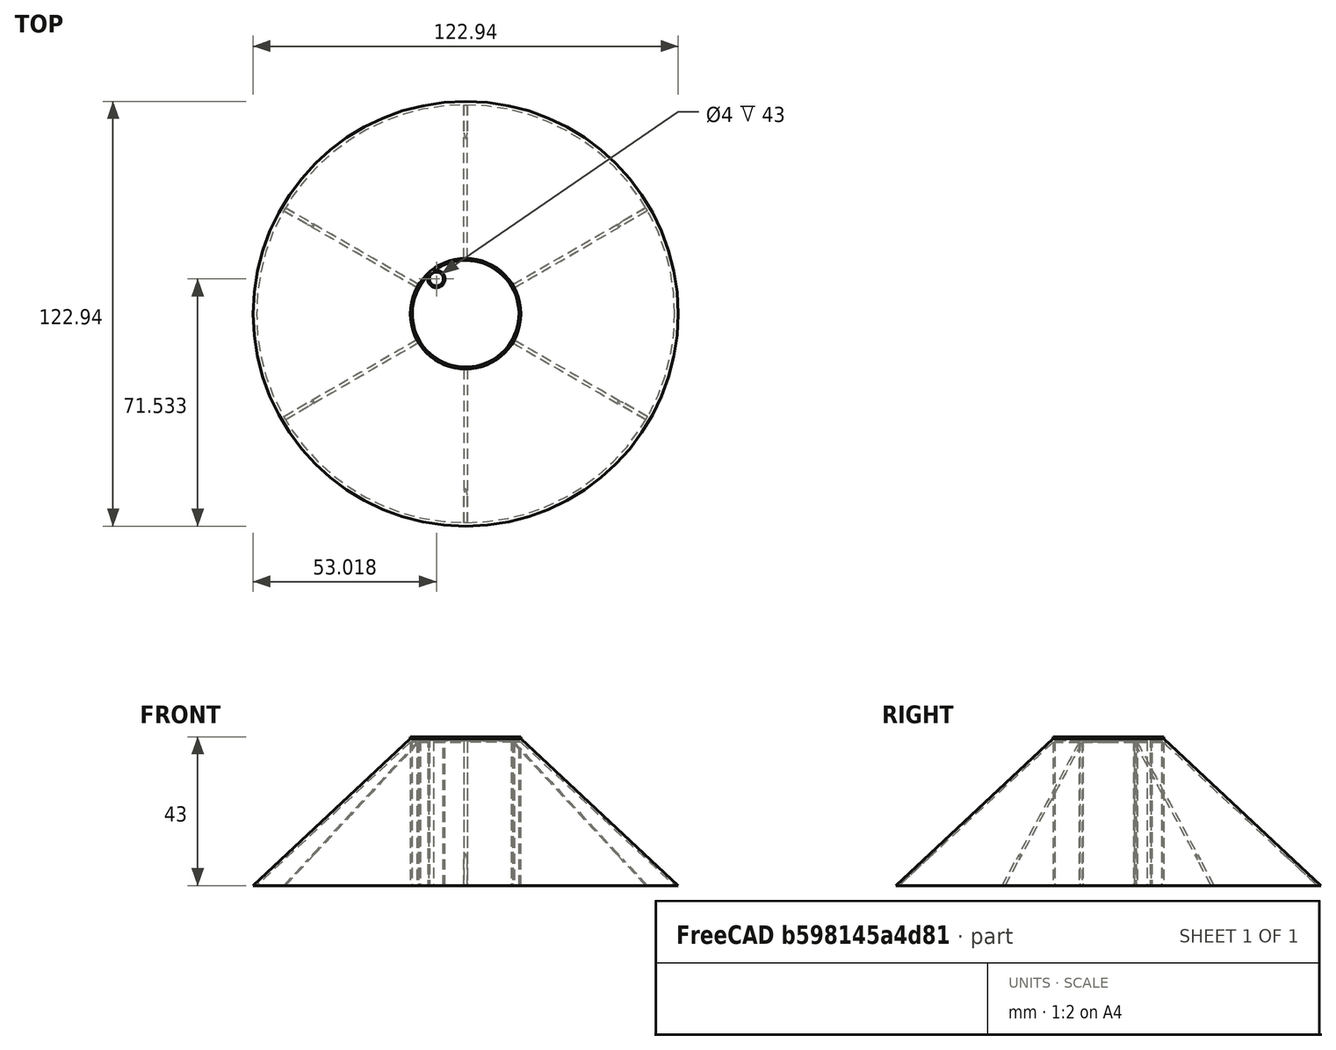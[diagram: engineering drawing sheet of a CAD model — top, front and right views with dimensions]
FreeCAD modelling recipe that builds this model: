
FCSTD DOCUMENT  (FreeCAD 0.20R29603 (Git))
Label: Ez3D-Mini-SaucerX2
License: All rights reserved
LicenseURL: http://en.wikipedia.org/wiki/All_rights_reserved
objects: Sketcher::SketchObject×4, PartDesign::Pad×3, Mesh::Feature×2, PartDesign::PolarPattern×1, PartDesign::Revolution×1, PartDesign::Body×1
note: 14 computed .brp shape members not serialized (recipe doc carries the construction recipe); baked Part::Feature solids carry a one-line shape summary decoded from their .brp

FEATURE [Mesh::Feature] Ez3D_13mmMotorTubeOnly_Body  label="Ez3D-13mmMotorTubeOnly-Body"
  Placement = pos=(-7.5,0,0) rot=(0,0,1;0rad)
FEATURE [Mesh::Feature] Ez3D_13mmMotorTubeOnly_Body001  label="Ez3D-13mmMotorTubeOnly-Body001"
  Placement = pos=(7.5,0,0) rot=(0,0,1;0rad)
FEATURE [Sketcher::SketchObject] Sketch  label="Center Support Structure"
  FullyConstrained = true
  MapMode = 5
  Support = -> [XY_Plane]
  sketch-geometry (2):
    g0: Circle CenterX=0 CenterY=0 CenterZ=0 NormalX=0 NormalY=0 NormalZ=1 AngleXU=0 Radius=15.5
    g1: Circle CenterX=0 CenterY=0 CenterZ=0 NormalX=0 NormalY=0 NormalZ=1 AngleXU=0 Radius=16
  constraints (4):
    c: Coincident(g0,g-1)
    c: Coincident(g1,g0)
    c: Diameter(g0) = 31
    c: Diameter(g1) = 32
FEATURE [PartDesign::Pad] Pad
  Direction = (0,0,1)
  Length = 43
  Length2 = 10
  Profile = -> Sketch
  ReferenceAxis = -> Sketch [N_Axis]
  Type = 0
FEATURE [Sketcher::SketchObject] Sketch001  label=""Fins""
  FullyConstrained = true
  MapMode = 5
  Placement = pos=(0,0,0) rot=(0.57735,0.57735,0.57735;2.0944rad)
  Support = -> [YZ_Plane]
  sketch-geometry (3):
    g0: LineSegment StartX=15.455 StartY=42 StartZ=0 EndX=15.455 EndY=0 EndZ=0
    g1: LineSegment StartX=15.455 StartY=0 StartZ=0 EndX=60.455 EndY=0 EndZ=0
    g2: LineSegment StartX=60.455 StartY=0 StartZ=0 EndX=15.455 EndY=42 EndZ=0
  constraints (9):
    c: Vertical(g0)
    c: Coincident(g0,g1)
    c: PointOnObject(g1,g-1)
    c: Horizontal(g1)
    c: Coincident(g1,g2)
    c: Coincident(g2,g0)
    c: DistanceY(g0,g0) = 42
    c: DistanceX(g-1,g0) = 15.455
    c: DistanceX(g1,g1) = 45
FEATURE [PartDesign::Pad] Pad001
  BaseFeature = -> Pad
  Direction = (1,-2e-16,3e-16)
  Length = 1
  Length2 = 10
  Midplane = true
  Profile = -> Sketch001
  ReferenceAxis = -> Sketch001 [N_Axis]
  Type = 0
FEATURE [PartDesign::PolarPattern] PolarPattern
  Angle = 360
  Axis = -> Z_Axis
  BaseFeature = -> Pad001
  Occurrences = 6
  Originals = -> [Pad001]
FEATURE [Sketcher::SketchObject] Sketch002  label="Top"
  FullyConstrained = false
  MapMode = 5
  Placement = pos=(0,0,0) rot=(0.57735,0.57735,0.57735;2.0944rad)
  Support = -> [YZ_Plane]
  sketch-geometry (4):
    g0: LineSegment StartX=15.445 StartY=42.9655 StartZ=0 EndX=15.445 EndY=41.9655 EndZ=0
    g1: LineSegment StartX=15.445 StartY=41.9655 StartZ=0 EndX=60.468 EndY=0 EndZ=0
    g2: LineSegment StartX=60.468 StartY=0 StartZ=0 EndX=61.468 EndY=0 EndZ=0
    g3: LineSegment StartX=61.468 StartY=0 StartZ=0 EndX=15.445 EndY=42.9655 EndZ=0
  constraints (9):
    c: Coincident(g0,g1)
    c: PointOnObject(g1,g-1)
    c: Coincident(g1,g2)
    c: PointOnObject(g2,g-1)
    c: Coincident(g2,g3)
    c: Coincident(g3,g0)
    c: DistanceX(g2,g2) = 1
    c: Vertical(g0)
    c: DistanceY(g0,g0) = 1
FEATURE [PartDesign::Revolution] Revolution
  Angle = 360
  Axis = (-2e-16,3e-16,1)
  Base = (0,0,0)
  BaseFeature = -> PolarPattern
  Profile = -> Sketch002
  ReferenceAxis = -> Sketch002 [V_Axis]
  Reversed = true
FEATURE [Sketcher::SketchObject] Sketch003
  FullyConstrained = false
  MapMode = 5
  Support = -> [XY_Plane]
  sketch-geometry (2):
    g0: Circle CenterX=-8.45241 CenterY=10.0631 CenterZ=0 NormalX=0 NormalY=0 NormalZ=1 AngleXU=0 Radius=2.5
    g1: Circle CenterX=-8.45241 CenterY=10.0631 CenterZ=0 NormalX=0 NormalY=0 NormalZ=1 AngleXU=0 Radius=2
  constraints (3):
    c: Coincident(g1,g0)
    c: Diameter(g0) = 5
    c: Diameter(g1) = 4
FEATURE [PartDesign::Pad] Pad002
  BaseFeature = -> Revolution
  Direction = (0,0,1)
  Length = 43
  Length2 = 10
  Profile = -> Sketch003
  ReferenceAxis = -> Sketch003 [N_Axis]
  Type = 0
FEATURE [PartDesign::Body] Body
  Group = -> [Sketch,Pad,Sketch001,Pad001,PolarPattern,Sketch002,Revolution,Sketch003,Pad002]
  Origin = -> Origin
  Tip = -> Pad002
